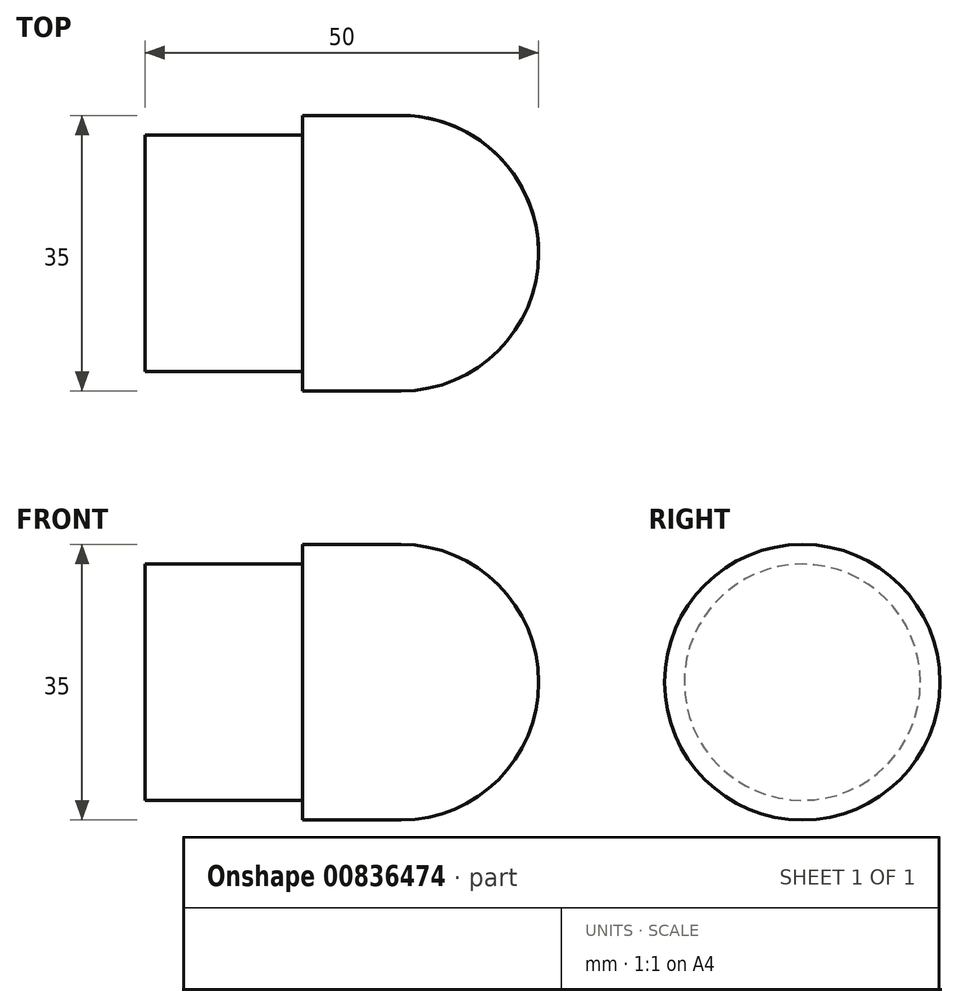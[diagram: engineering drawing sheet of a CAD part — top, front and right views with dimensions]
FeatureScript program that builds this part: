
annotation { "Feature Type Name" : "Feature", "Feature Type Description" : "" }
export const myFeature = defineFeature(function(context is Context, id is Id, definition is map)
    precondition{}
    {
        {
            var Q0;
            Q0=qCreatedBy(makeId("Top.planeOp"),FACE);
            var sketch = newSketch(context, id + "F0", { "sketchPlane" : qUnion([Q0])});
            skLineSegment(sketch, "E0.bottom", {"start": v(0, 0) * mm, "end": v(20, 0) * mm});
            skLineSegment(sketch, "E0.top", {"start": v(0, 15) * mm, "end": v(20, 15) * mm});
            skLineSegment(sketch, "E0.left", {"start": v(0, 0) * mm, "end": v(0, 15) * mm});
            skLineSegment(sketch, "E0.right", {"start": v(20, 0) * mm, "end": v(20, 15) * mm});
            skArc(sketch, "E1", {"start": v(50, 0) * mm, "mid": v(44.87, 12.37) * mm, "end": v(32.5, 17.5) * mm});
            skLineSegment(sketch, "E2", {"start": v(32.5, 17.5) * mm, "end": v(32.5, 0) * mm});
            skLineSegment(sketch, "E3.bottom", {"start": v(32.5, 17.5) * mm, "end": v(20, 17.5) * mm});
            skLineSegment(sketch, "E3.top", {"start": v(32.5, 0) * mm, "end": v(20, 0) * mm});
            skLineSegment(sketch, "E3.right", {"start": v(20, 17.5) * mm, "end": v(20, 0) * mm});
            skLineSegment(sketch, "E4", {"start": v(32.5, 0) * mm, "end": v(56.07, 0) * mm});
            skSolve(sketch);
        }
        {
            var Q0;
            Q0 = qSketchRegion(id + "F0", true);
            var Q1;
            Q1=sQuery(id+"F0.wireOp",EDGE,"E0.bottom");
            revolve(context, id + "F1", {"surfaceOperationType" : NewSurfaceOperationType.NEW, "entities" : qUnion([Q0]), "axis" : qUnion([Q1]), "revolveType" : RevolveType.FULL});
        }
    });
